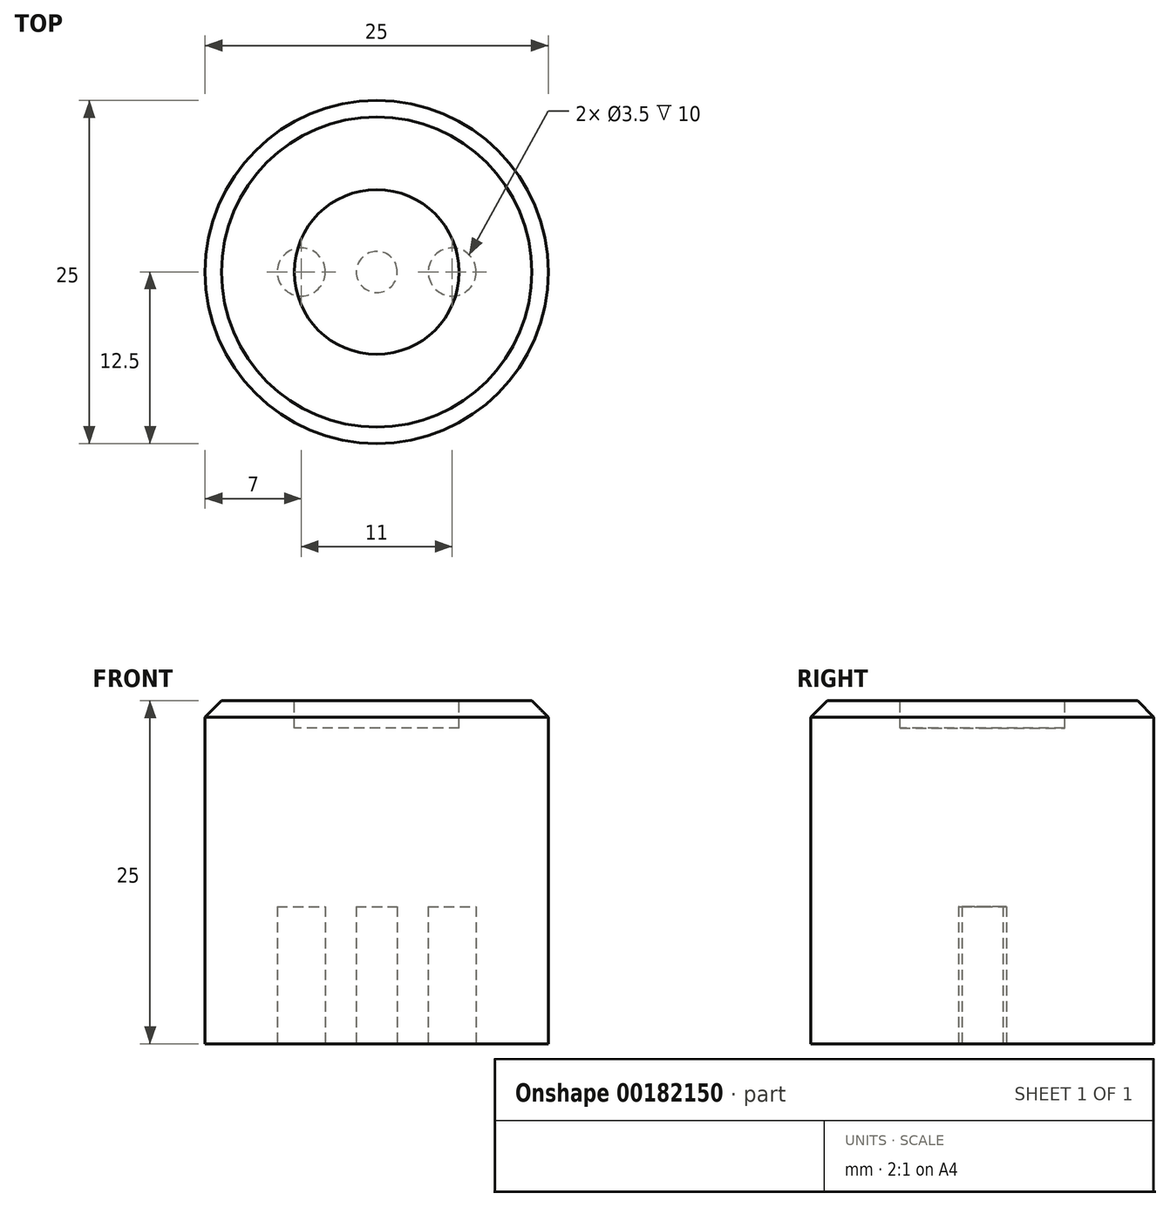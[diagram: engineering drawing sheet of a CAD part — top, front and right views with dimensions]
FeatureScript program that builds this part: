
annotation { "Feature Type Name" : "Feature", "Feature Type Description" : "" }
export const myFeature = defineFeature(function(context is Context, id is Id, definition is map)
    precondition{}
    {
        {
            var Q0;
            Q0=qCreatedBy(makeId("Top.planeOp"),FACE);
            var sketch = newSketch(context, id + "F0", { "sketchPlane" : qUnion([Q0])});
            skCircle(sketch, "E0", {"center": v(0, 0) * mm, "radius": 12.5 * mm});
            skSolve(sketch);
        }
        {
            var Q0;
            Q0 = qSketchRegion(id + "F0", true);
            extrude(context, id + "F1", {"entities" : qUnion([Q0]), "depth" : 25 * mm});
        }
        {
            var Q0;
            Q0=makeQuery(id+"F1.opExtrude","CAP_FACE",FACE,{"disambiguationData":[OSD([sQuery(id+"F0.wireOp",EDGE,"E0")])],"isStart":false});
            var sketch = newSketch(context, id + "F2", { "sketchPlane" : qUnion([Q0])});
            skCircle(sketch, "E1", {"center": v(0, 0) * mm, "radius": 6 * mm});
            skSolve(sketch);
        }
        {
            var Q0;
            Q0 = qSketchRegion(id + "F2", true);
            extrude(context, id + "F3", {"entities" : qUnion([Q0]), "operationType" : NewBodyOperationType.REMOVE, "oppositeDirection" : true, "depth" : 2 * mm});
        }
        {
            var Q0;
            Q0=makeQuery(id+"F1.opExtrude","CAP_FACE",FACE,{"disambiguationData":[OSD([sQuery(id+"F0.wireOp",EDGE,"E0")])],"isStart":true});
            var sketch = newSketch(context, id + "F4", { "sketchPlane" : qUnion([Q0])});
            skLineSegment(sketch, "E2", {"start": v(-12.5, 0) * mm, "end": v(12.5, 0) * mm});
            skCircle(sketch, "E3", {"center": v(0, 0) * mm, "radius": 1.5 * mm});
            skCircle(sketch, "E4", {"center": v(5.5, 0) * mm, "radius": 1.75 * mm});
            skCircle(sketch, "E5", {"center": v(-5.5, 0) * mm, "radius": 1.75 * mm});
            skSolve(sketch);
        }
        {
            var Q0;
            Q0 = qSketchRegion(id + "F4", true);
            extrude(context, id + "F5", {"entities" : qUnion([Q0]), "operationType" : NewBodyOperationType.REMOVE, "oppositeDirection" : true, "depth" : 10 * mm});
        }
        {
            var Q0;
            Q0=makeQuery(id+"F1.opExtrude","CAP_EDGE",EDGE,{"disambiguationData":[OSD([sQuery(id+"F0.wireOp",EDGE,"E0")])],"isStart":false});
            chamfer(context, id + "F6", {"entities" : qUnion([Q0]), "width" : 1.2 * mm, "tangentPropagation" : true});
        }
    });
